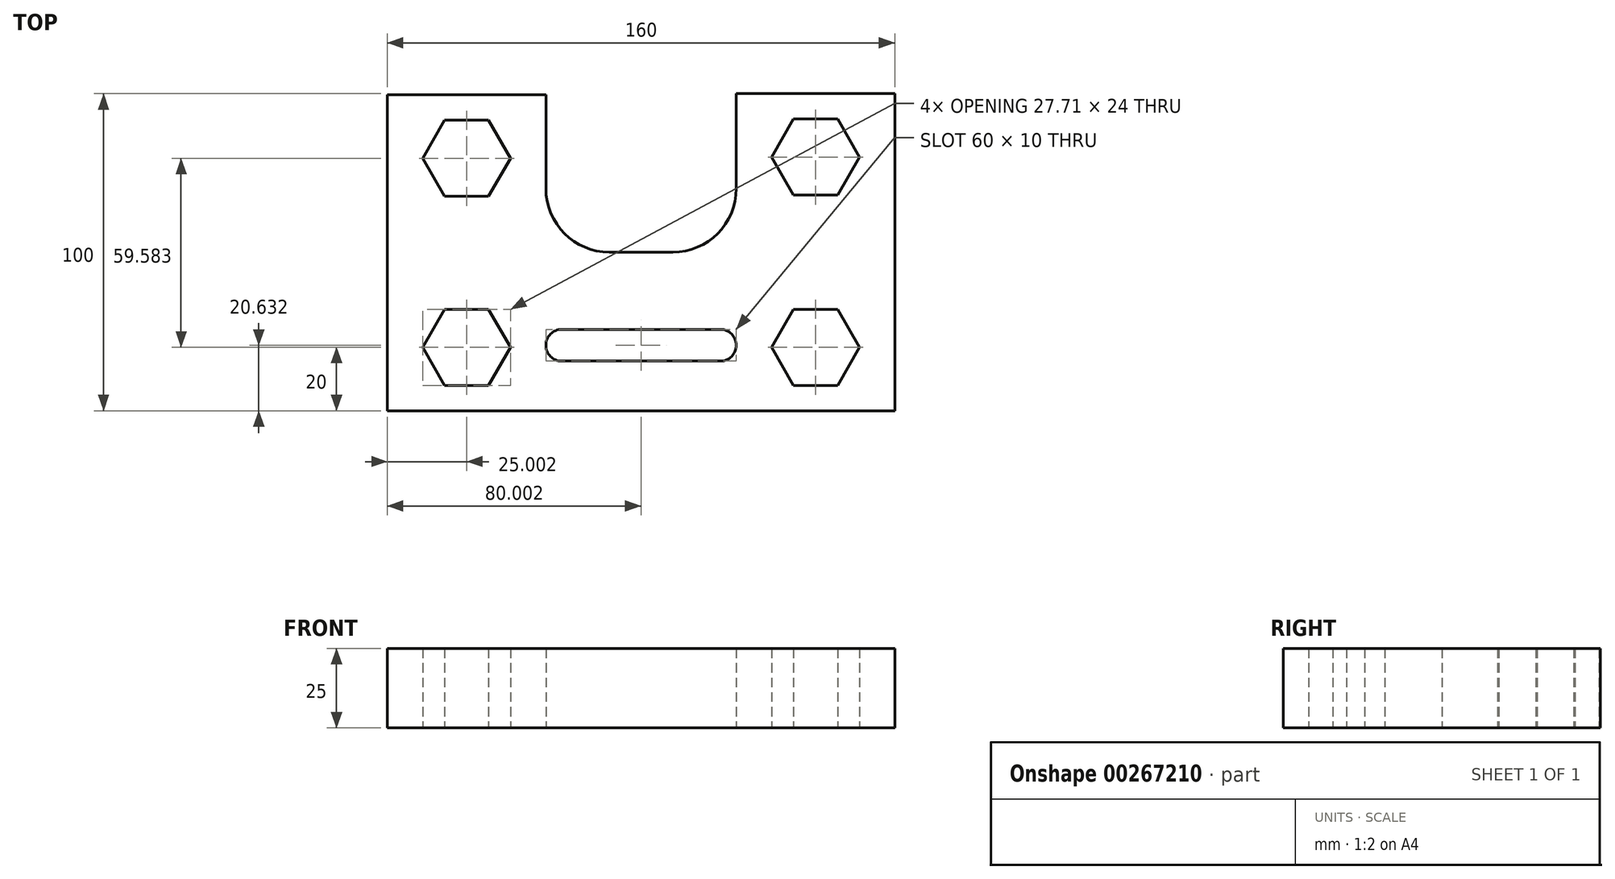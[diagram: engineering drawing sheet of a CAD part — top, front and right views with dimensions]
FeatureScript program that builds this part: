
annotation { "Feature Type Name" : "Feature", "Feature Type Description" : "" }
export const myFeature = defineFeature(function(context is Context, id is Id, definition is map)
    precondition{}
    {
        {
            var Q0;
            Q0=qCreatedBy(makeId("Top.planeOp"),FACE);
            var sketch = newSketch(context, id + "F0", { "sketchPlane" : qUnion([Q0])});
            skLineSegment(sketch, "E0", {"start": v(-85.74, -50) * mm, "end": v(74.26, -50) * mm});
            skLineSegment(sketch, "E1", {"start": v(74.26, -50) * mm, "end": v(74.26, 50) * mm});
            skLineSegment(sketch, "E2", {"start": v(74.26, 50) * mm, "end": v(24.26, 50) * mm});
            skLineSegment(sketch, "E3", {"start": v(24.26, 50) * mm, "end": v(24.26, 20) * mm});
            skLineSegment(sketch, "E4", {"start": v(4.26, 0) * mm, "end": v(-15.74, 0) * mm});
            skLineSegment(sketch, "E5", {"start": v(-35.74, 20) * mm, "end": v(-35.74, 49.58) * mm});
            skLineSegment(sketch, "E6", {"start": v(-35.74, 49.58) * mm, "end": v(-85.74, 49.58) * mm});
            skLineSegment(sketch, "E7", {"start": v(-85.74, 49.58) * mm, "end": v(-85.74, -50) * mm});
            skPoint(sketch, "E8.visualSharp", {"position": v(-35.74, 0) * mm});
            skArc(sketch, "E8.filletArc", {"start": v(-35.74, 20) * mm, "mid": v(-29.88, 5.86) * mm, "end": v(-15.74, 0) * mm});
            skPoint(sketch, "E9.visualSharp", {"position": v(24.26, 0) * mm});
            skArc(sketch, "E9.filletArc", {"start": v(4.26, 0) * mm, "mid": v(18.4, 5.86) * mm, "end": v(24.26, 20) * mm});
            skLineSegment(sketch, "E10", {"start": v(-85.74, -50) * mm, "end": v(-30.74, -50) * mm});
            skLineSegment(sketch, "E11", {"start": v(-30.74, -50) * mm, "end": v(19.26, -50) * mm});
            skLineSegment(sketch, "E12", {"start": v(74.26, -50) * mm, "end": v(74.26, -30) * mm});
            skLineSegment(sketch, "E13", {"start": v(74.26, -30) * mm, "end": v(-85.74, -30) * mm, "construction": true});
            skLineSegment(sketch, "E14", {"start": v(-30.74, -50) * mm, "end": v(-30.74, -18.53) * mm, "construction": true});
            skLineSegment(sketch, "E15", {"start": v(19.26, -50) * mm, "end": v(19.26, -16.65) * mm, "construction": true});
            skLineSegment(sketch, "E16", {"start": v(-30.74, -24.37) * mm, "end": v(19.26, -24.37) * mm});
            skLineSegment(sketch, "E17", {"start": v(19.26, -34.37) * mm, "end": v(-30.74, -34.37) * mm});
            skArc(sketch, "E18", {"start": v(-30.74, -24.37) * mm, "mid": v(-35.74, -29.37) * mm, "end": v(-30.74, -34.37) * mm});
            skArc(sketch, "E19", {"start": v(19.26, -34.37) * mm, "mid": v(24.26, -29.37) * mm, "end": v(19.26, -24.37) * mm});
            skLineSegment(sketch, "E20", {"start": v(74.26, -30) * mm, "end": v(49.26, -30) * mm});
            skLineSegment(sketch, "E21", {"start": v(-85.74, -30) * mm, "end": v(-60.74, -30) * mm});
            skCircle(sketch, "E22.cCircle", {"center": v(-60.74, -30) * mm, "radius": 12 * mm, "construction": true});
            skLineSegment(sketch, "E22.0", {"start": v(-74.6, -30) * mm, "end": v(-67.67, -18) * mm});
            skLineSegment(sketch, "E22.1", {"start": v(-67.67, -18) * mm, "end": v(-53.8, -18) * mm});
            skLineSegment(sketch, "E22.2", {"start": v(-53.8, -18) * mm, "end": v(-46.88, -30) * mm});
            skLineSegment(sketch, "E22.3", {"start": v(-46.88, -30) * mm, "end": v(-53.8, -42) * mm});
            skLineSegment(sketch, "E22.4", {"start": v(-53.8, -42) * mm, "end": v(-67.67, -42) * mm});
            skLineSegment(sketch, "E22.5", {"start": v(-67.67, -42) * mm, "end": v(-74.6, -30) * mm});
            skPoint(sketch, "E22.0.midPoint", {"position": v(-71.13, -24) * mm});
            skCircle(sketch, "E23.cCircle", {"center": v(49.26, -30) * mm, "radius": 12 * mm, "construction": true});
            skLineSegment(sketch, "E23.0", {"start": v(35.4, -30) * mm, "end": v(42.33, -18) * mm});
            skLineSegment(sketch, "E23.1", {"start": v(42.33, -18) * mm, "end": v(56.2, -18) * mm});
            skLineSegment(sketch, "E23.2", {"start": v(56.2, -18) * mm, "end": v(63.12, -30) * mm});
            skLineSegment(sketch, "E23.3", {"start": v(63.12, -30) * mm, "end": v(56.2, -42) * mm});
            skLineSegment(sketch, "E23.4", {"start": v(56.2, -42) * mm, "end": v(42.33, -42) * mm});
            skLineSegment(sketch, "E23.5", {"start": v(42.33, -42) * mm, "end": v(35.4, -30) * mm});
            skPoint(sketch, "E23.0.midPoint", {"position": v(38.87, -24) * mm});
            skLineSegment(sketch, "E24", {"start": v(-60.74, -30) * mm, "end": v(-60.74, 49.58) * mm, "construction": true});
            skLineSegment(sketch, "E25", {"start": v(49.26, -30) * mm, "end": v(49.26, 50) * mm, "construction": true});
            skLineSegment(sketch, "E26", {"start": v(49.26, 50) * mm, "end": v(49.26, 30) * mm});
            skLineSegment(sketch, "E27", {"start": v(-60.74, 49.58) * mm, "end": v(-60.74, 29.58) * mm});
            skCircle(sketch, "E28.cCircle", {"center": v(-60.74, 29.58) * mm, "radius": 12 * mm, "construction": true});
            skLineSegment(sketch, "E28.0", {"start": v(-74.6, 29.58) * mm, "end": v(-67.67, 41.58) * mm});
            skLineSegment(sketch, "E28.1", {"start": v(-67.67, 41.58) * mm, "end": v(-53.8, 41.58) * mm});
            skLineSegment(sketch, "E28.2", {"start": v(-53.8, 41.58) * mm, "end": v(-46.88, 29.58) * mm});
            skLineSegment(sketch, "E28.3", {"start": v(-46.88, 29.58) * mm, "end": v(-53.8, 17.58) * mm});
            skLineSegment(sketch, "E28.4", {"start": v(-53.8, 17.58) * mm, "end": v(-67.67, 17.58) * mm});
            skLineSegment(sketch, "E28.5", {"start": v(-67.67, 17.58) * mm, "end": v(-74.6, 29.58) * mm});
            skPoint(sketch, "E28.0.midPoint", {"position": v(-71.13, 35.58) * mm});
            skCircle(sketch, "E29.cCircle", {"center": v(49.26, 30) * mm, "radius": 12 * mm, "construction": true});
            skLineSegment(sketch, "E29.0", {"start": v(56.2, 42) * mm, "end": v(63.12, 30) * mm});
            skLineSegment(sketch, "E29.1", {"start": v(63.12, 30) * mm, "end": v(56.2, 18) * mm});
            skLineSegment(sketch, "E29.2", {"start": v(56.2, 18) * mm, "end": v(42.33, 18) * mm});
            skLineSegment(sketch, "E29.3", {"start": v(42.33, 18) * mm, "end": v(35.4, 30) * mm});
            skLineSegment(sketch, "E29.4", {"start": v(35.4, 30) * mm, "end": v(42.33, 42) * mm});
            skLineSegment(sketch, "E29.5", {"start": v(42.33, 42) * mm, "end": v(56.2, 42) * mm});
            skPoint(sketch, "E29.0.midPoint", {"position": v(59.65, 36) * mm});
            skSolve(sketch);
        }
        {
            var Q0;
            Q0 = qSketchRegion(id + "F0", true);
            extrude(context, id + "F1", {"entities" : qUnion([Q0]), "depth" : 25 * mm});
        }
    });
